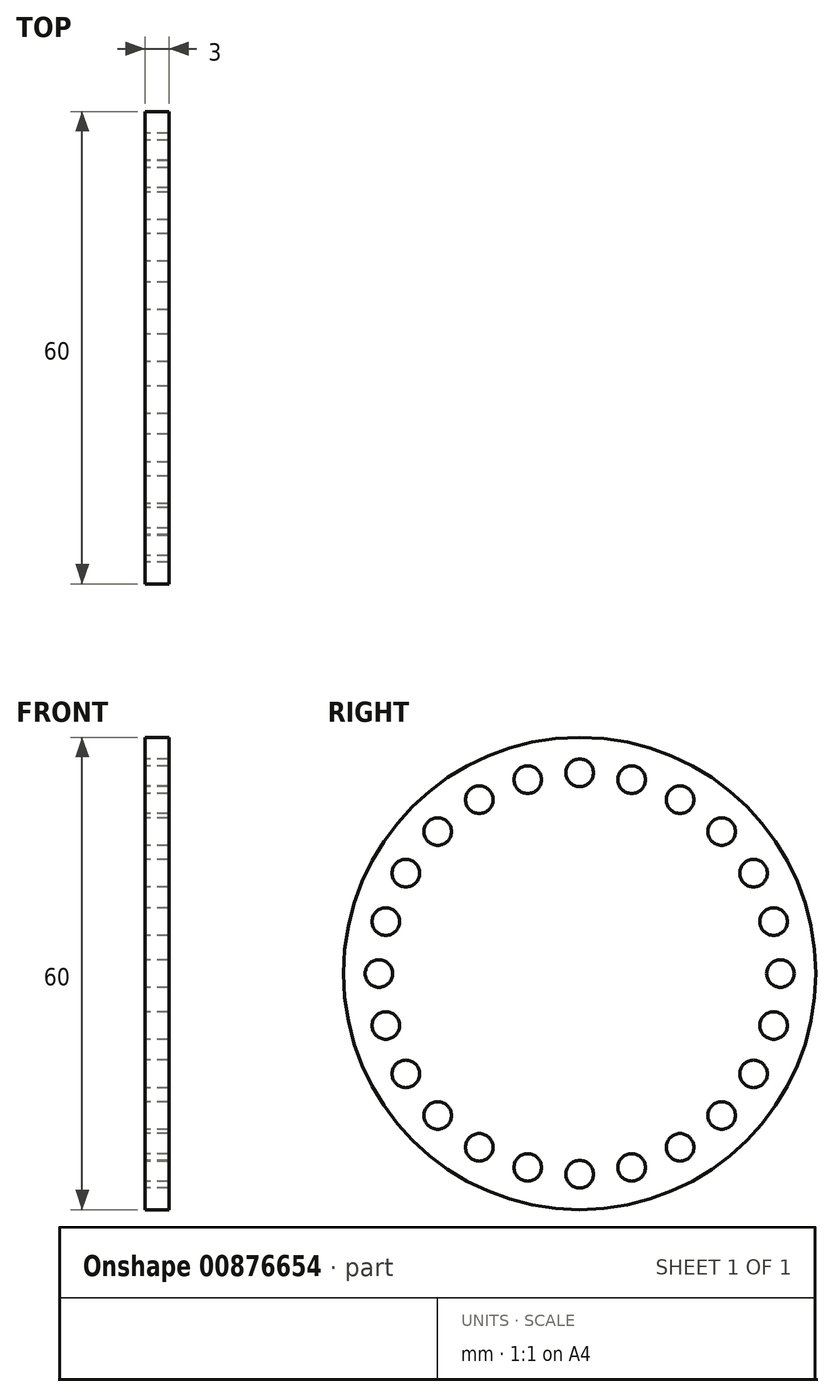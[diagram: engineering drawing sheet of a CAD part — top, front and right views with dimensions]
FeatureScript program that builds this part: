
annotation { "Feature Type Name" : "Feature", "Feature Type Description" : "" }
export const myFeature = defineFeature(function(context is Context, id is Id, definition is map)
    precondition{}
    {
        {
            var Q0;
            Q0=qCreatedBy(makeId("Right.planeOp"),FACE);
            var sketch = newSketch(context, id + "F0", { "sketchPlane" : qUnion([Q0])});
            skCircle(sketch, "E0", {"center": v(0, 0) * mm, "radius": 30 * mm});
            skCircle(sketch, "E1", {"center": v(-25.5, 0) * mm, "radius": 1.75 * mm});
            skCircle(sketch, "E2.1.0", {"center": v(-24.63, -6.6) * mm, "radius": 1.75 * mm});
            skCircle(sketch, "E2.2.0", {"center": v(-22.08, -12.75) * mm, "radius": 1.75 * mm});
            skCircle(sketch, "E2.3.0", {"center": v(-18.03, -18.03) * mm, "radius": 1.75 * mm});
            skCircle(sketch, "E2.4.0", {"center": v(-12.75, -22.08) * mm, "radius": 1.75 * mm});
            skCircle(sketch, "E2.5.0", {"center": v(-6.6, -24.63) * mm, "radius": 1.75 * mm});
            skCircle(sketch, "E2.6.0", {"center": v(0, -25.5) * mm, "radius": 1.75 * mm});
            skCircle(sketch, "E2.7.0", {"center": v(6.6, -24.63) * mm, "radius": 1.75 * mm});
            skCircle(sketch, "E2.8.0", {"center": v(12.75, -22.08) * mm, "radius": 1.75 * mm});
            skCircle(sketch, "E2.9.0", {"center": v(18.03, -18.03) * mm, "radius": 1.75 * mm});
            skCircle(sketch, "E2.10.0", {"center": v(22.08, -12.75) * mm, "radius": 1.75 * mm});
            skCircle(sketch, "E2.11.0", {"center": v(24.63, -6.6) * mm, "radius": 1.75 * mm});
            skCircle(sketch, "E2.12.0", {"center": v(25.5, 0) * mm, "radius": 1.75 * mm});
            skCircle(sketch, "E2.13.0", {"center": v(24.63, 6.6) * mm, "radius": 1.75 * mm});
            skCircle(sketch, "E2.14.0", {"center": v(22.08, 12.75) * mm, "radius": 1.75 * mm});
            skCircle(sketch, "E2.15.0", {"center": v(18.03, 18.03) * mm, "radius": 1.75 * mm});
            skCircle(sketch, "E2.16.0", {"center": v(12.75, 22.08) * mm, "radius": 1.75 * mm});
            skCircle(sketch, "E2.17.0", {"center": v(6.6, 24.63) * mm, "radius": 1.75 * mm});
            skCircle(sketch, "E2.18.0", {"center": v(0, 25.5) * mm, "radius": 1.75 * mm});
            skCircle(sketch, "E2.19.0", {"center": v(-6.6, 24.63) * mm, "radius": 1.75 * mm});
            skCircle(sketch, "E2.20.0", {"center": v(-12.75, 22.08) * mm, "radius": 1.75 * mm});
            skCircle(sketch, "E2.21.0", {"center": v(-18.03, 18.03) * mm, "radius": 1.75 * mm});
            skCircle(sketch, "E2.22.0", {"center": v(-22.08, 12.75) * mm, "radius": 1.75 * mm});
            skCircle(sketch, "E2.23.0", {"center": v(-24.63, 6.6) * mm, "radius": 1.75 * mm});
            skSolve(sketch);
        }
        {
            var Q0;
            Q0=makeQuery(id+"F0.imprint","IMPRINT",FACE,{"disambiguationData":[TD([[makeQuery(id+"F0.imprint","IMPRINT",EDGE,{"derivedFrom":sQuery(id+"F0.wireOp",EDGE,"E0")}),1.0]])]});
            extrude(context, id + "F1", {"entities" : qUnion([Q0]), "depth" : 3 * mm, "offsetDistance" : 25 * mm});
        }
    });
